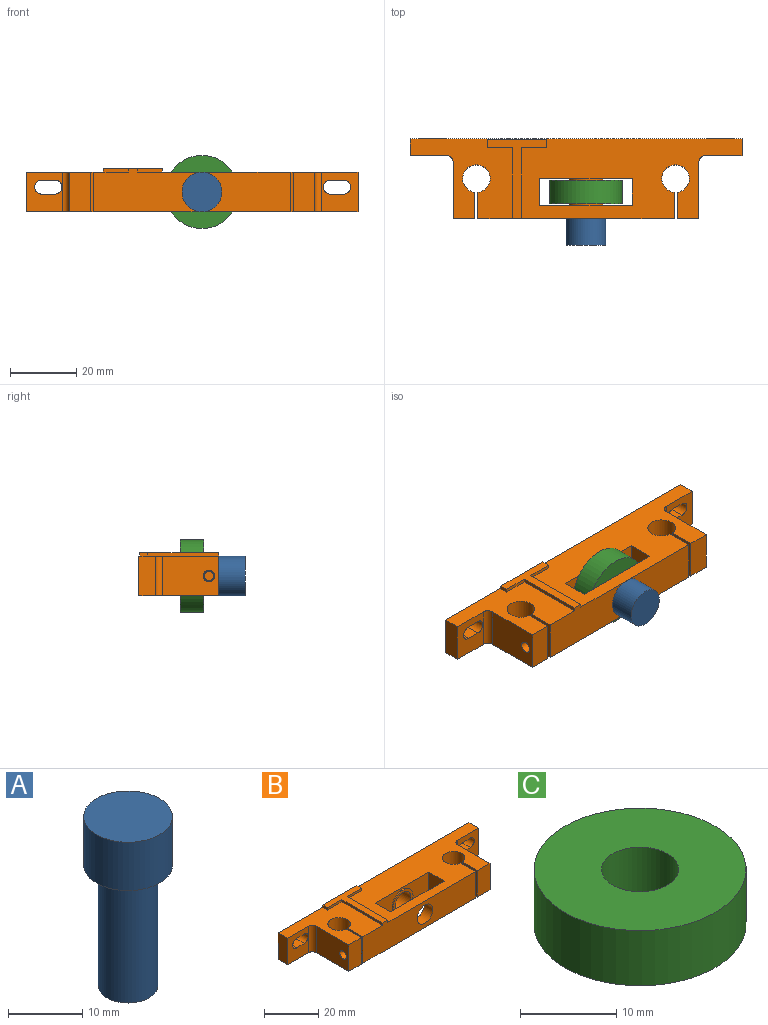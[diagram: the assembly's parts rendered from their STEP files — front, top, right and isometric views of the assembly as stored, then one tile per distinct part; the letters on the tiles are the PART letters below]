
ASSEMBLY  parts=3 mates=2
PART A: 5 faces, bbox 12x12x28 mm
  f0: cylinder r=4mm len=20mm, axis (0,0,-1), area 502.7mm2, adj f1,f4
  f1: plane 8x8mm, normal (0,0,-1), area 50.3mm2, adj f0
  f2: cylinder r=6mm len=12mm, axis (0,0,-1), area 301.6mm2, adj f3,f4
  f3: plane 12x12mm, normal (0,0,1), area 113.1mm2, adj f2
  f4: plane 12x12mm, normal (0,0,-1), area 62.8mm2, adj f0,f2
PART B: 53 faces, bbox 100x24x13 mm
  f0: plane 100x24mm, normal (0,0,1), area 1458.9mm2, adj f2,f3,f4,f5,f6,f7,f8,f9
  f1: plane 100x24mm, normal (0,0,-1), area 1561.7mm2, adj f2,f3,f4,f5,f6,f7,f8,f9
  f2: plane 100x12mm, normal (0,1,0), area 1138.7mm2, adj f0,f1,f6,f11,f18,f19,f20,f21
  f3: plane 12x11mm, normal (0,-1,0), area 101.3mm2, adj f0,f1,f11,f22,f23,f24,f25,f48
  f4: plane 12x6.56mm, normal (0,-1,0), area 78.7mm2, adj f0,f1,f10,f16
  f5: plane 59.12x13mm, normal (0,-1,0), area 659.4mm2, adj f0,f1,f14,f17,f26,f37,f38,f44
  f6: plane 12x5mm, normal (-1,0,0), area 60mm2, adj f0,f1,f2,f7
  f7: plane 12x11mm, normal (0,-1,0), area 101.3mm2, adj f0,f1,f6,f18,f19,f20,f21,f52
  f8: plane 17x12mm, normal (-1,0,0), area 194.9mm2, adj f0,f1,f9,f51,f52
  f9: plane 12x6.56mm, normal (0,-1,0), area 78.7mm2, adj f0,f1,f8,f13
  f10: plane 17x12mm, normal (1,0,0), area 194.9mm2, adj f0,f1,f4,f47,f48
  f11: plane 12x5mm, normal (1,0,0), area 60mm2, adj f0,f1,f2,f3
  f12: cylinder r=4.15mm len=12mm, axis (0,0,1), area 302.4mm2, adj f0,f1,f13,f14
  f13: plane 12x7.87mm, normal (1,0,0), area 85.4mm2, adj f0,f1,f9,f12,f51
  f14: plane 12x7.87mm, normal (-1,0,0), area 88.3mm2, adj f0,f1,f5,f12,f50
  f15: cylinder r=4.15mm len=12mm, axis (0,0,1), area 302.4mm2, adj f0,f1,f16,f17
  f16: plane 12x7.87mm, normal (-1,0,0), area 85.4mm2, adj f0,f1,f4,f15,f47
  f17: plane 12x7.87mm, normal (1,0,0), area 88.3mm2, adj f0,f1,f5,f15,f46
  f18: cylinder r=2.1mm len=5mm, axis (0,1,0), area 33mm2, adj f2,f7,f19,f21
  f19: plane 5x4mm, normal (0,0,1), area 20mm2, adj f2,f7,f18,f20
  f20: cylinder r=2.1mm len=5mm, axis (0,1,0), area 33mm2, adj f2,f7,f19,f21
  f21: plane 5x4mm, normal (0,0,-1), area 20mm2, adj f2,f7,f18,f20
  f22: plane 5x4mm, normal (0,0,-1), area 20mm2, adj f2,f3,f23,f25
  f23: cylinder r=2.1mm len=5mm, axis (0,1,0), area 33mm2, adj f2,f3,f22,f24
  f24: plane 5x4mm, normal (0,0,1), area 20mm2, adj f2,f3,f23,f25
  f25: cylinder r=2.1mm len=5mm, axis (0,1,0), area 33mm2, adj f2,f3,f22,f24
  f26: cylinder r=4.1mm len=8.2mm, axis (0,-1,0), area 115.9mm2, adj f5,f36
  f27: plane 12x8mm, normal (1,0,0), area 96mm2, adj f0,f1,f29,f30
  f28: plane 12x8mm, normal (-1,0,0), area 96mm2, adj f0,f1,f29,f30
  f29: plane 28x12mm, normal (0,-1,0), area 251.2mm2, adj f0,f1,f27,f28,f31
  f30: plane 28x12mm, normal (0,1,0), area 249.3mm2, adj f0,f1,f27,f28,f35
  f31: cylinder r=5.2mm len=10.39mm, axis (0,1,0), area 16.3mm2, adj f29,f32
  f32: plane 10.39x10.39mm, normal (0,-1,0), area 32mm2, adj f31,f34
  f33: plane 8.2x8.2mm, normal (0,-1,0), area 52.8mm2, adj f34
  f34: cylinder r=4.1mm len=8.5mm, axis (0,-1,0), area 219mm2, adj f32,f33
  f35: cylinder r=5.25mm len=10.51mm, axis (0,-1,0), area 16.5mm2, adj f30,f36
  f36: plane 10.51x10.51mm, normal (0,1,0), area 33.9mm2, adj f26,f35
  f37: plane 21.34x1mm, normal (-1,0,0), area 21.3mm2, adj f0,f5,f43,f44
  f38: plane 21.34x1mm, normal (1,0,0), area 21.3mm2, adj f0,f5,f39,f44
  f39: plane 7.54x1mm, normal (0,-1,0), area 7.5mm2, adj f0,f38,f40,f44
  f40: plane 2.46x1mm, normal (1,0,0), area 2.5mm2, adj f0,f39,f41,f44
  f41: plane 17.84x1mm, normal (0,1,0), area 17.8mm2, adj f0,f40,f42,f44
  f42: plane 2.46x1mm, normal (-1,0,0), area 2.5mm2, adj f0,f41,f43,f44
  f43: plane 7.54x1mm, normal (0,-1,0), area 7.5mm2, adj f0,f37,f42,f44
  f44: plane 23.8x17.84mm, normal (0,0,1), area 102.9mm2, adj f5,f37,f38,f39,f40,f41,f42,f43
  f45: plane 2.8x2.8mm, normal (1,0,0), area 6.2mm2, adj f46
  f46: cylinder r=1.4mm len=10.56mm, axis (1,0,0), area 92.9mm2, adj f17,f45
  f47: cylinder r=1.7mm len=6.56mm, axis (1,0,0), area 70.1mm2, adj f10,f16
  f48: cylinder r=2mm len=12mm, axis (0,0,1), area 37.7mm2, adj f0,f1,f3,f10
  f49: plane 2.8x2.8mm, normal (-1,0,0), area 6.2mm2, adj f50
  f50: cylinder r=1.4mm len=10.56mm, axis (-1,0,0), area 92.9mm2, adj f14,f49
  f51: cylinder r=1.7mm len=6.56mm, axis (-1,0,0), area 70.1mm2, adj f8,f13
  f52: cylinder r=2mm len=12mm, axis (0,0,1), area 37.7mm2, adj f0,f1,f7,f8
PART C: 4 faces, bbox 22x22x7 mm
  f0: cylinder r=4mm len=8mm, axis (0,0,-1), area 175.9mm2, adj f2,f3
  f1: cylinder r=11mm len=22mm, axis (0,0,-1), area 483.8mm2, adj f2,f3
  f2: plane 22x22mm, normal (0,0,1), area 329.9mm2, adj f0,f1
  f3: plane 22x22mm, normal (0,0,-1), area 329.9mm2, adj f0,f1
PLACE A rot(axis=(1,0,0),90deg) t=(5.95,13.74,6.05)mm
PLACE B t=(-0.7,5.43,0.05)mm
PLACE C rot(axis=(-1,0,0),90deg) t=(5.95,-1.76,6.05)mm
MATE fastened C.f0 <-> B.f26  axis (0,1,0) through (5.95,5.24,6.05)mm
MATE fastened A.f0 <-> B.f26  axis (0,1,0) through (5.95,-6.26,6.05)mm
